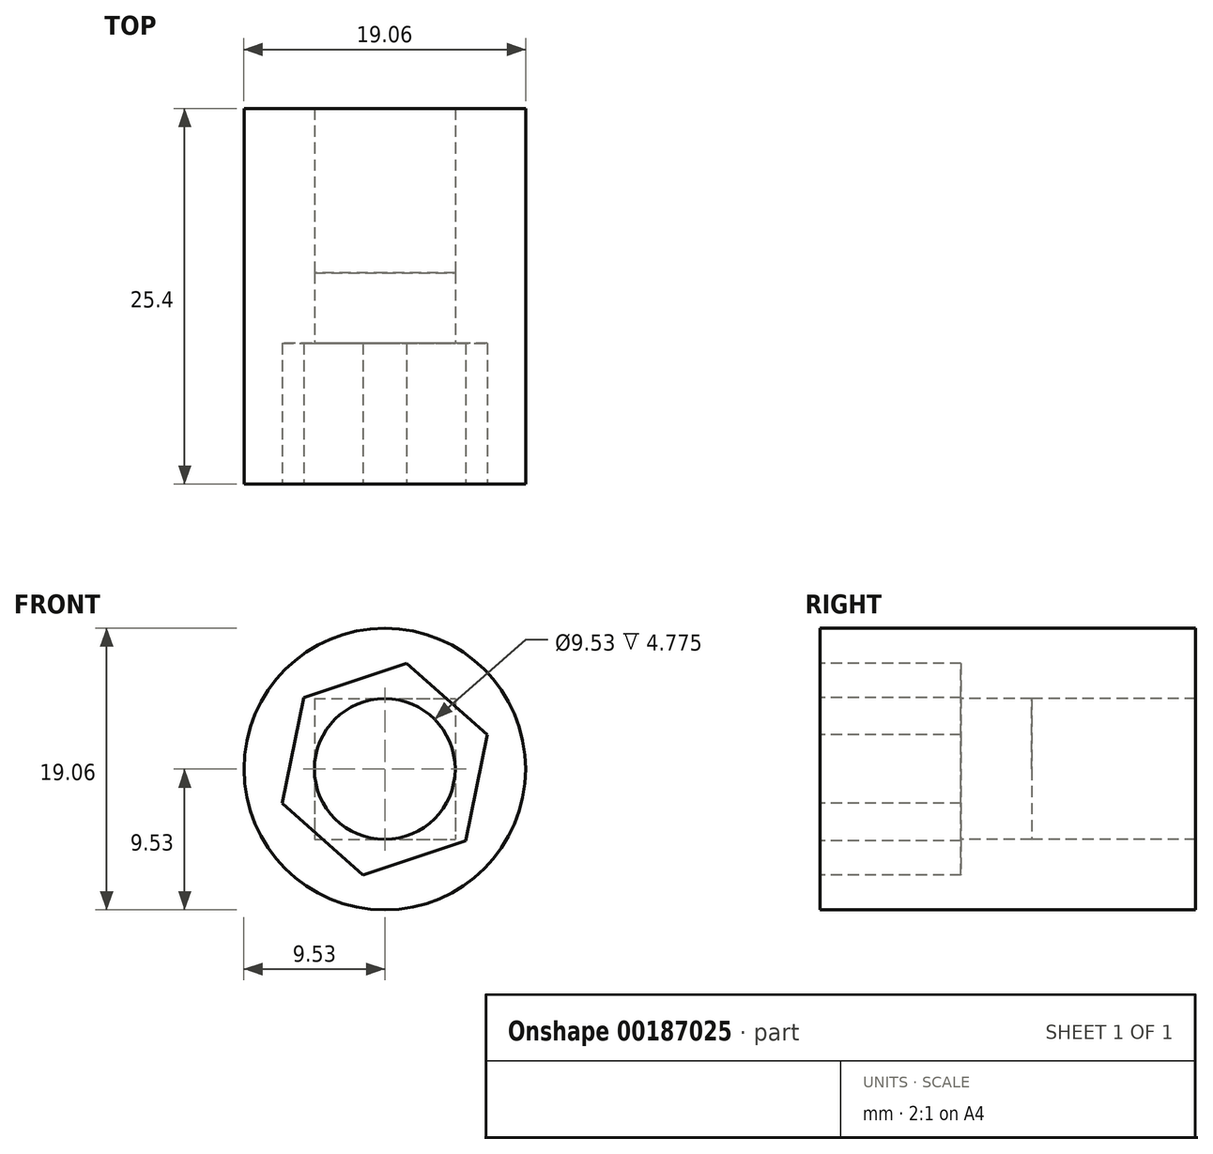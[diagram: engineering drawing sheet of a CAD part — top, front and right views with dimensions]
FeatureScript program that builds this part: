
annotation { "Feature Type Name" : "Feature", "Feature Type Description" : "" }
export const myFeature = defineFeature(function(context is Context, id is Id, definition is map)
    precondition{}
    {
        {
            var Q0;
            Q0=qCreatedBy(makeId("Front.planeOp"),FACE);
            var sketch = newSketch(context, id + "F0", { "sketchPlane" : qUnion([Q0])});
            skCircle(sketch, "E0", {"center": v(0, 0) * mm, "radius": 9.53 * mm});
            skSolve(sketch);
        }
        {
            var Q0;
            Q0 = qSketchRegion(id + "F0", true);
            var Q1;
            Q1=makeQuery(id+"F0.imprint","IMPRINT",FACE,{"disambiguationData":[TD([[makeQuery(id+"F0.imprint","IMPRINT",EDGE,{"derivedFrom":sQuery(id+"F0.wireOp",EDGE,"E0")}),1.0]])]});
            extrude(context, id + "F1", {"entities" : qUnion([Q0, Q1]), "depth" : 25.4 * mm});
        }
        {
            var Q0;
            Q0=qCreatedBy(makeId("Front.planeOp"),FACE);
            var sketch = newSketch(context, id + "F2", { "sketchPlane" : qUnion([Q0])});
            skLineSegment(sketch, "E1.bottom", {"start": v(-4.76, 4.76) * mm, "end": v(4.76, 4.76) * mm});
            skLineSegment(sketch, "E1.top", {"start": v(-4.76, -4.76) * mm, "end": v(4.76, -4.76) * mm});
            skLineSegment(sketch, "E1.left", {"start": v(-4.76, 4.76) * mm, "end": v(-4.76, -4.76) * mm});
            skLineSegment(sketch, "E1.right", {"start": v(4.76, 4.76) * mm, "end": v(4.76, -4.76) * mm});
            skPoint(sketch, "E1.middle", {"position": v(0, 0) * mm});
            skCircle(sketch, "E2", {"center": v(0, 0) * mm, "radius": 4.76 * mm});
            skSolve(sketch);
        }
        {
            var Q0;
            {var subQ0=sQuery(id+"F2.wireOp",EDGE,"E2");var subQ1=makeQuery(id+"F2.imprint","INTERSECT",VERTEX,{"derivedFrom":[sQuery(id+"F2.wireOp",EDGE,"E1.bottom"),subQ0]});Q0=makeQuery(id+"F2.imprint","IMPRINT",FACE,{"disambiguationData":[TD([[makeQuery(id+"F2.imprint","IMPRINT",EDGE,{"disambiguationData":[TD([[subQ1,1.0]])],"derivedFrom":subQ0}),1.0]])]});}
            extrude(context, id + "F3", {"entities" : qUnion([Q0]), "operationType" : NewBodyOperationType.REMOVE, "endBound" : BoundingType.THROUGH_ALL, "oppositeDirection" : true, "depth" : 25.4 * mm, "hasSecondDirection" : true, "secondDirectionOppositeDirection" : false, "secondDirectionDepth" : 25.4 * mm});
        }
        {
            var Q0;
            Q0 = qSketchRegion(id + "F2", true);
            extrude(context, id + "F4", {"entities" : qUnion([Q0]), "operationType" : NewBodyOperationType.REMOVE, "oppositeDirection" : true, "depth" : 11.1 * mm, "hasSecondDirection" : true, "secondDirectionOppositeDirection" : false, "secondDirectionDepth" : 11.1 * mm});
        }
        {
            var Q0;
            Q0=makeQuery(id+"F1.opExtrude","CAP_FACE",FACE,{"disambiguationData":[OSD([sQuery(id+"F0.wireOp",EDGE,"E0")])],"isStart":false});
            var sketch = newSketch(context, id + "F5", { "sketchPlane" : qUnion([Q0])});
            skCircle(sketch, "E3.cCircle", {"center": v(0, 0) * mm, "radius": 6.32 * mm, "construction": true});
            skLineSegment(sketch, "E3.0", {"start": v(-5.46, 4.84) * mm, "end": v(1.46, 7.15) * mm});
            skLineSegment(sketch, "E3.1", {"start": v(1.46, 7.15) * mm, "end": v(6.93, 2.3) * mm});
            skLineSegment(sketch, "E3.2", {"start": v(6.93, 2.3) * mm, "end": v(5.46, -4.84) * mm});
            skLineSegment(sketch, "E3.3", {"start": v(5.46, -4.84) * mm, "end": v(-1.46, -7.15) * mm});
            skLineSegment(sketch, "E3.4", {"start": v(-1.46, -7.15) * mm, "end": v(-6.93, -2.3) * mm});
            skLineSegment(sketch, "E3.5", {"start": v(-6.93, -2.3) * mm, "end": v(-5.46, 4.84) * mm});
            skPoint(sketch, "E3.0.midPoint", {"position": v(-2, 6) * mm});
            skSolve(sketch);
        }
        {
            var Q0;
            Q0 = qSketchRegion(id + "F5", true);
            extrude(context, id + "F6", {"entities" : qUnion([Q0]), "operationType" : NewBodyOperationType.REMOVE, "oppositeDirection" : true, "depth" : 9.52 * mm});
        }
    });
